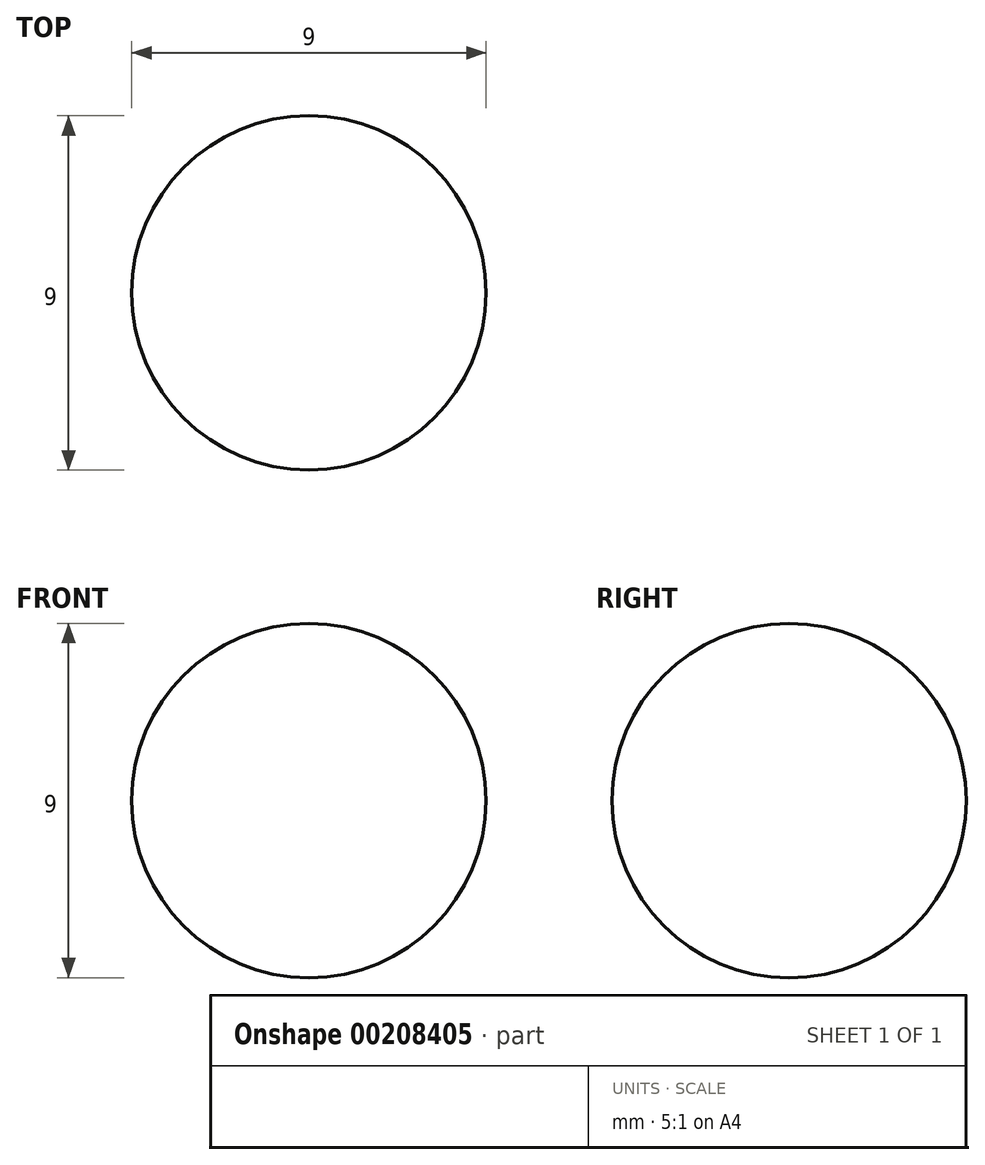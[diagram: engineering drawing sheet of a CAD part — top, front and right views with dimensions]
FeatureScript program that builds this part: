
annotation { "Feature Type Name" : "Feature", "Feature Type Description" : "" }
export const myFeature = defineFeature(function(context is Context, id is Id, definition is map)
    precondition{}
    {
        {
            var Q0;
            Q0=qCreatedBy(makeId("Front.planeOp"),FACE);
            var sketch = newSketch(context, id + "F0", { "sketchPlane" : qUnion([Q0])});
            skCircle(sketch, "E0", {"center": v(0, 0) * mm, "radius": 4.5 * mm});
            skSolve(sketch);
        }
        {
            var Q0;
            Q0=makeQuery(id+"F0.imprint","IMPRINT",FACE,{"disambiguationData":[TD([[makeQuery(id+"F0.imprint","IMPRINT",EDGE,{"derivedFrom":sQuery(id+"F0.wireOp",EDGE,"E0")}),1.0]])]});
            extrude(context, id + "F1", {"entities" : qUnion([Q0]), "oppositeDirection" : true, "depth" : 9 * mm, "symmetric" : true});
        }
        {
            var Q0;
            Q0=makeQuery(id+"F1.opExtrude","CAP_EDGE",EDGE,{"disambiguationData":[OSD([sQuery(id+"F0.wireOp",EDGE,"E0")])],"isStart":false});
            var Q1;
            Q1=makeQuery(id+"F1.opExtrude","CAP_EDGE",EDGE,{"disambiguationData":[OSD([sQuery(id+"F0.wireOp",EDGE,"E0")])],"isStart":true});
            var Q2;
            Q2=makeQuery(id+"F1.opExtrude","CAP_EDGE",EDGE,{"disambiguationData":[OSD([sQuery(id+"F0.wireOp",EDGE,"E0")])],"isStart":true});
            var Q3;
            Q3=makeQuery(id+"F1.opExtrude","CAP_EDGE",EDGE,{"disambiguationData":[OSD([sQuery(id+"F0.wireOp",EDGE,"E0")])],"isStart":false});
            fillet(context, id + "F2", {"entities" : qUnion([Q0, Q1, Q2, Q3]), "radius" : 4.5 * mm, "allowEdgeOverflow" : false});
        }
    });
